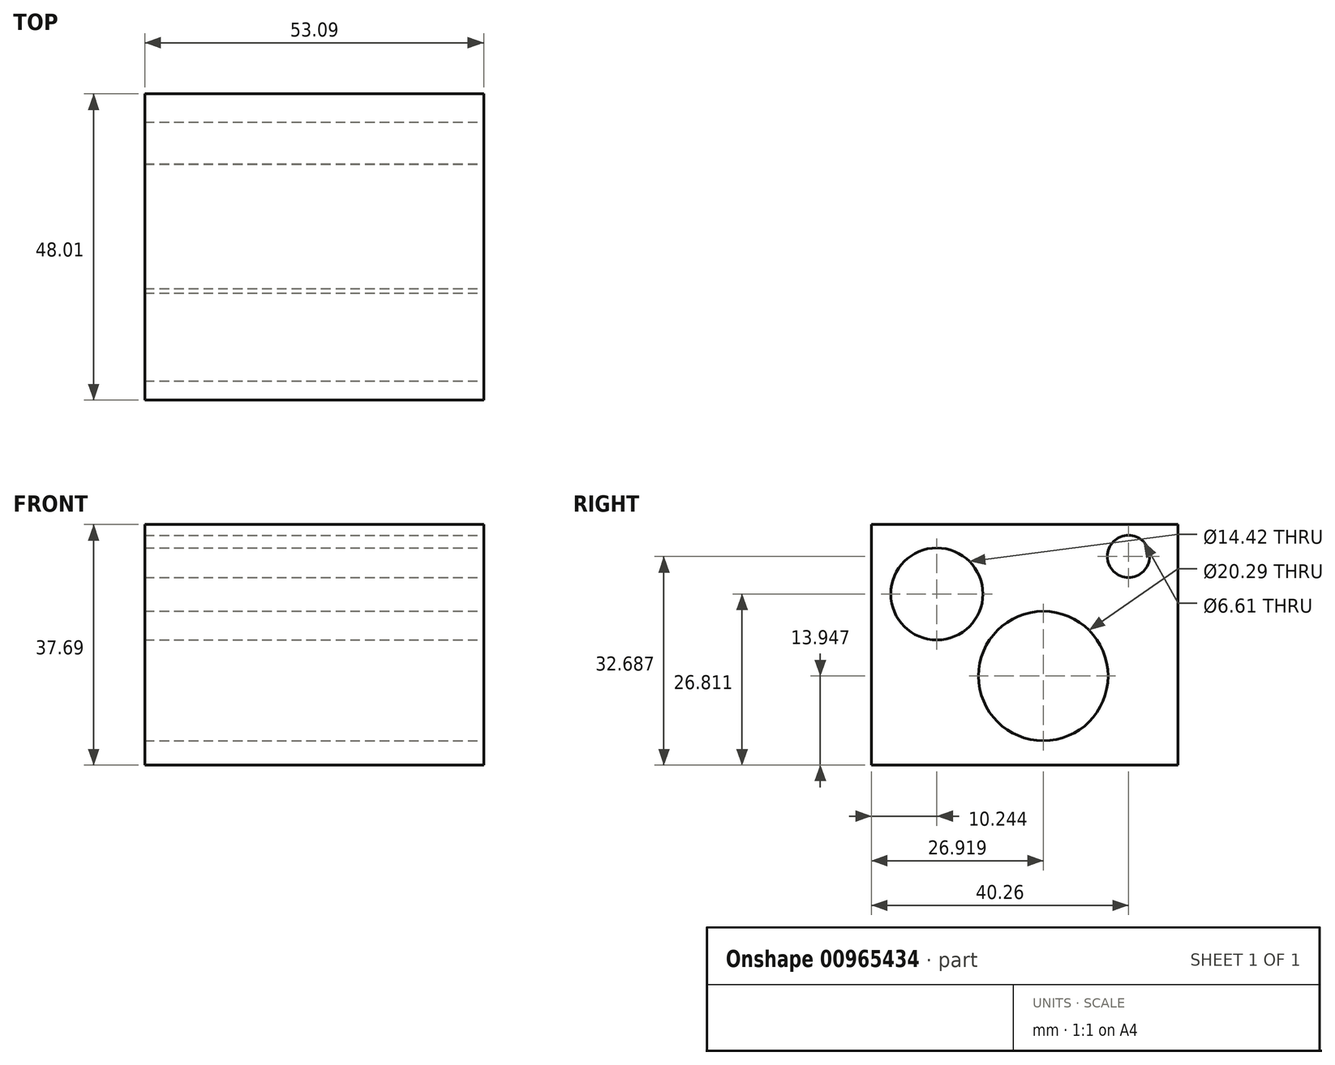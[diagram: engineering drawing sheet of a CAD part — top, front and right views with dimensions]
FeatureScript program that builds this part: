
annotation { "Feature Type Name" : "Feature", "Feature Type Description" : "" }
export const myFeature = defineFeature(function(context is Context, id is Id, definition is map)
    precondition{}
    {
        {
            var Q0;
            Q0=qCreatedBy(makeId("Right.planeOp"),FACE);
            var sketch = newSketch(context, id + "F0", { "sketchPlane" : qUnion([Q0])});
            skLineSegment(sketch, "E0.bottom", {"start": v(0, 0) * mm, "end": v(48, 0) * mm});
            skLineSegment(sketch, "E0.top", {"start": v(0, -37.69) * mm, "end": v(48, -37.69) * mm});
            skLineSegment(sketch, "E0.left", {"start": v(0, 0) * mm, "end": v(0, -37.69) * mm});
            skLineSegment(sketch, "E0.right", {"start": v(48, 0) * mm, "end": v(48, -37.69) * mm});
            skSolve(sketch);
        }
        {
            var Q0;
            Q0=makeQuery(id+"F0.imprint","IMPRINT",FACE,{"disambiguationData":[TD([[makeQuery(id+"F0.imprint","IMPRINT",EDGE,{"derivedFrom":sQuery(id+"F0.wireOp",EDGE,"E0.bottom")}),-1.0]])]});
            extrude(context, id + "F1", {"entities" : qUnion([Q0]), "depth" : 53.1 * mm, "offsetDistance" : 25.4 * mm});
        }
        {
            var Q0;
            Q0=makeQuery(id+"F1.opExtrude","CAP_FACE",FACE,{"disambiguationData":[OSD([sQuery(id+"F0.wireOp",EDGE,"E0.bottom"),sQuery(id+"F0.wireOp",EDGE,"E0.top"),sQuery(id+"F0.wireOp",EDGE,"E0.left"),sQuery(id+"F0.wireOp",EDGE,"E0.right")])],"isStart":false});
            var sketch = newSketch(context, id + "F2", { "sketchPlane" : qUnion([Q0])});
            skCircle(sketch, "E1", {"center": v(10.24, -10.88) * mm, "radius": 7.2 * mm});
            skCircle(sketch, "E2", {"center": v(26.92, -23.74) * mm, "radius": 10.15 * mm});
            skCircle(sketch, "E3", {"center": v(40.26, -5) * mm, "radius": 3.3 * mm});
            skSolve(sketch);
        }
        {
            var Q0;
            Q0=makeQuery(id+"F2.imprint","IMPRINT",FACE,{"disambiguationData":[TD([[makeQuery(id+"F2.imprint","IMPRINT",EDGE,{"derivedFrom":sQuery(id+"F2.wireOp",EDGE,"E1")}),1.0]])]});
            var Q1;
            Q1=makeQuery(id+"F2.imprint","IMPRINT",FACE,{"disambiguationData":[TD([[makeQuery(id+"F2.imprint","IMPRINT",EDGE,{"derivedFrom":sQuery(id+"F2.wireOp",EDGE,"E2")}),1.0]])]});
            var Q2;
            Q2=makeQuery(id+"F2.imprint","IMPRINT",FACE,{"disambiguationData":[TD([[makeQuery(id+"F2.imprint","IMPRINT",EDGE,{"derivedFrom":sQuery(id+"F2.wireOp",EDGE,"E3")}),1.0]])]});
            extrude(context, id + "F3", {"entities" : qUnion([Q0, Q1, Q2]), "operationType" : NewBodyOperationType.REMOVE, "endBound" : BoundingType.THROUGH_ALL, "oppositeDirection" : true, "depth" : 25.4 * mm, "offsetDistance" : 25.4 * mm});
        }
    });
